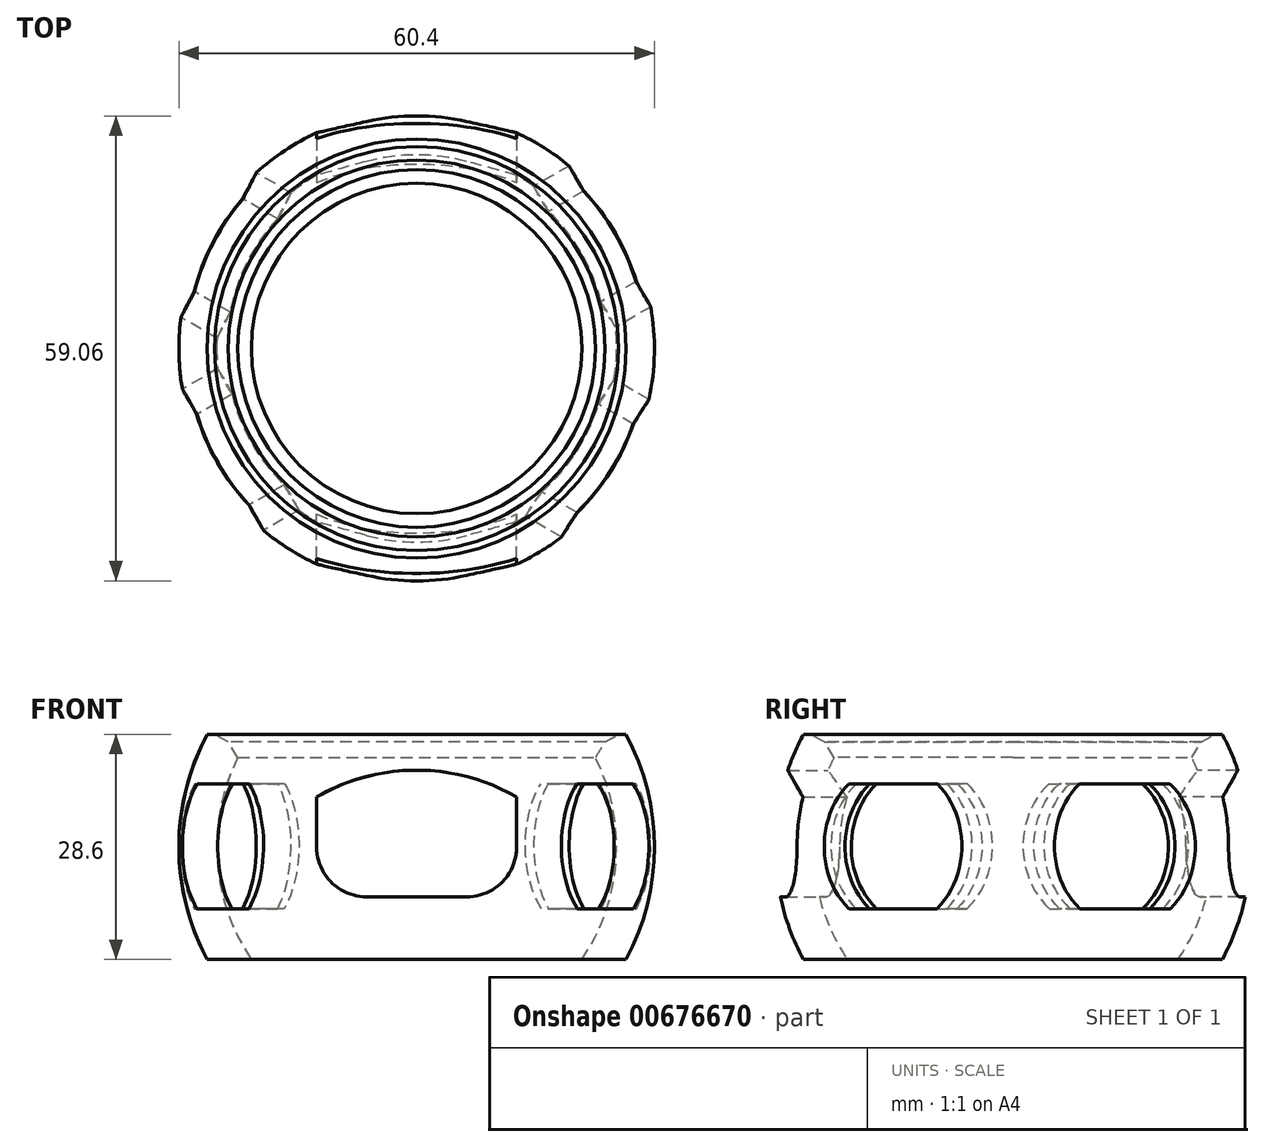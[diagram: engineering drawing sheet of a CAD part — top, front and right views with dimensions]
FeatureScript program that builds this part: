
annotation { "Feature Type Name" : "Feature", "Feature Type Description" : "" }
export const myFeature = defineFeature(function(context is Context, id is Id, definition is map)
    precondition{}
    {
        {
            var Q0;
            Q0=qCreatedBy(makeId("Front.planeOp"),FACE);
            var sketch = newSketch(context, id + "F0", { "sketchPlane" : qUnion([Q0])});
            skArc(sketch, "E0", {"start": v(26.6, -14.3) * mm, "mid": v(30.2, 0) * mm, "end": v(26.6, 14.3) * mm});
            skArc(sketch, "E1", {"start": v(21, -14.3) * mm, "mid": v(25.4, 0) * mm, "end": v(21, 14.3) * mm});
            skLineSegment(sketch, "E2", {"start": v(21, 14.3) * mm, "end": v(26.6, 14.3) * mm});
            skLineSegment(sketch, "E3", {"start": v(21, -14.3) * mm, "end": v(26.6, -14.3) * mm});
            skLineSegment(sketch, "E4", {"start": v(0, 0) * mm, "end": v(0, 43.57) * mm});
            skSolve(sketch);
        }
        {
            var Q0;
            Q0=makeQuery(id+"F0.imprint","IMPRINT",FACE,{"disambiguationData":[TD([[makeQuery(id+"F0.imprint","IMPRINT",EDGE,{"derivedFrom":sQuery(id+"F0.wireOp",EDGE,"E0")}),1.0]])]});
            var Q1;
            Q1=sQuery(id+"F0.wireOp",EDGE,"E4");
            revolve(context, id + "F1", {"entities" : qUnion([Q0]), "axis" : qUnion([Q1]), "revolveType" : RevolveType.FULL});
        }
        {
            var Q0;
            Q0=qCreatedBy(makeId("Top.planeOp"),FACE);
            var sketch = newSketch(context, id + "F2", { "sketchPlane" : qUnion([Q0])});
            skCircle(sketch, "E5", {"center": v(0, 0) * mm, "radius": 23.02 * mm});
            skSolve(sketch);
        }
        {
            var Q0;
            Q0=makeQuery(id+"F1.opRevolve","SWEPT_EDGE",EDGE,{"disambiguationData":[OSD([sQuery(id+"F0.wireOp",EDGE,"E1"),sQuery(id+"F0.wireOp",EDGE,"E2")])]});
            chamfer(context, id + "F3", {"entities" : qUnion([Q0]), "width" : 2.03 * mm, "tangentPropagation" : true});
        }
        {
            var Q0;
            {var subQ0=sQuery(id+"F0.wireOp",EDGE,"E2");Q0=makeQuery(id+"F3.opChamfer","BLEND_EDGE",EDGE,{"blendedFrom":[makeQuery(id+"F1.opRevolve","SWEPT_EDGE",EDGE,{"disambiguationData":[OSD([sQuery(id+"F0.wireOp",EDGE,"E1"),subQ0])]}),makeQuery(id+"F1.opRevolve","SWEPT_FACE",FACE,{"disambiguationData":[OSD([subQ0])]})],"blendedInto":[makeQuery(id+"F1.opRevolve","SWEPT_FACE",FACE,{"disambiguationData":[OSD([subQ0])]})]});}
            chamfer(context, id + "F4", {"entities" : qUnion([Q0]), "width" : 2.03 * mm, "tangentPropagation" : true});
        }
        {
            var Q0;
            Q0=qCreatedBy(makeId("Front.planeOp"),FACE);
            var sketch = newSketch(context, id + "F5", { "sketchPlane" : qUnion([Q0])});
            skLineSegment(sketch, "E6", {"start": v(0, -14.29) * mm, "end": v(0, 0) * mm});
            skLineSegment(sketch, "E7", {"start": v(0, 0) * mm, "end": v(0, -6.35) * mm});
            skLineSegment(sketch, "E8", {"start": v(0, -6.35) * mm, "end": v(6.35, -6.35) * mm});
            skLineSegment(sketch, "E9", {"start": v(0, -6.35) * mm, "end": v(-6.35, -6.35) * mm});
            skLineSegment(sketch, "E10", {"start": v(-12.7, 0) * mm, "end": v(-12.7, 6.35) * mm});
            skLineSegment(sketch, "E11", {"start": v(12.7, 6.35) * mm, "end": v(12.7, 0) * mm});
            skArc(sketch, "E12", {"start": v(12.7, 6.35) * mm, "mid": v(0, 9.75) * mm, "end": v(-12.7, 6.35) * mm});
            skCircle(sketch, "E13", {"center": v(-6.35, 0) * mm, "radius": 6.35 * mm});
            skCircle(sketch, "E14", {"center": v(6.35, 0) * mm, "radius": 6.35 * mm});
            skPoint(sketch, "E15.orphan", {"position": v(-12.7, -6.35) * mm});
            skPoint(sketch, "E16.orphan", {"position": v(12.7, -6.35) * mm});
            skLineSegment(sketch, "E17", {"start": v(0, 0) * mm, "end": v(-1.81, 0) * mm});
            skSolve(sketch);
        }
        {
            var Q0;
            Q0 = qSketchRegion(id + "F5", true);
            extrude(context, id + "F6", {"entities" : qUnion([Q0]), "operationType" : NewBodyOperationType.REMOVE, "oppositeDirection" : true, "depth" : 76.2 * mm, "offsetDistance" : 25.4 * mm});
        }
        {
            var Q0;
            Q0 = qSketchRegion(id + "F5", true);
            extrude(context, id + "F7", {"entities" : qUnion([Q0]), "operationType" : NewBodyOperationType.REMOVE, "depth" : 76.2 * mm, "offsetDistance" : 25.4 * mm});
        }
        {
            var Q0;
            Q0=qCreatedBy(makeId("Top.planeOp"),FACE);
            var sketch = newSketch(context, id + "F8", { "sketchPlane" : qUnion([Q0])});
            skLineSegment(sketch, "E18", {"start": v(41.9, 24.28) * mm, "end": v(-40.53, -23.31) * mm});
            skLineSegment(sketch, "E19", {"start": v(-54.26, 31.56) * mm, "end": v(52.81, -30.26) * mm});
            skLineSegment(sketch, "E20", {"start": v(26.12, 15.16) * mm, "end": v(10, 43.08) * mm});
            skLineSegment(sketch, "E21", {"start": v(26.25, -14.93) * mm, "end": v(7.89, -46.74) * mm});
            skSolve(sketch);
        }
        {
            var Q0;
            Q0=sQuery(id+"F8.wireOp",EDGE,"E20");
            cPlane(context, id + "F9", {"entities" : qUnion([Q0]), "cplaneType" : CPlaneType.LINE_ANGLE, "offset" : 25.4 * mm, "angle" : 90 * degree, "width" : 152.4 * mm, "height" : 152.4 * mm});
        }
        {
            var Q0;
            Q0=qCreatedBy(id+"F9.planeOp",FACE);
            var sketch = newSketch(context, id + "F10", { "sketchPlane" : qUnion([Q0])});
            skArc(sketch, "E22", {"start": v(-6.59, 8.04) * mm, "mid": v(-10.3, 0.1) * mm, "end": v(-6.59, -7.84) * mm});
            skLineSegment(sketch, "E23", {"start": v(0.05, 0.1) * mm, "end": v(0.05, 8.04) * mm});
            skLineSegment(sketch, "E24", {"start": v(0.05, 0.1) * mm, "end": v(0.05, -7.84) * mm});
            skLineSegment(sketch, "E25", {"start": v(0.05, 8.04) * mm, "end": v(-6.59, 8.04) * mm});
            skLineSegment(sketch, "E26", {"start": v(-6.59, 8.04) * mm, "end": v(6.7, 8.04) * mm});
            skLineSegment(sketch, "E27", {"start": v(0.05, -7.84) * mm, "end": v(6.7, -7.84) * mm});
            skLineSegment(sketch, "E28", {"start": v(6.7, -7.84) * mm, "end": v(-6.59, -7.84) * mm});
            skArc(sketch, "E29.trimOffspring", {"start": v(6.7, -7.84) * mm, "mid": v(10.4, 0.1) * mm, "end": v(6.7, 8.04) * mm});
            skSolve(sketch);
        }
        {
            var Q0;
            {var subQ1=sQuery(id+"F10.wireOp",EDGE,"E22");Q0=makeQuery(id+"F10.imprint","IMPRINT",FACE,{"disambiguationData":[TD([[makeQuery(id+"F10.imprint","IMPRINT",EDGE,{"derivedFrom":subQ1}),1.0]])]});}
            var Q1;
            {var subQ4=sQuery(id+"F10.wireOp",EDGE,"E23");Q1=makeQuery(id+"F10.imprint","IMPRINT",FACE,{"disambiguationData":[TD([[makeQuery(id+"F10.imprint","IMPRINT",EDGE,{"derivedFrom":subQ4}),-1.0]])]});}
            var Q2;
            Q2 = qConstructionFilter(qBodyType(qCreatedBy(id + "F10" ,EDGE), BodyType.WIRE), ConstructionObject.NO);
            extrude(context, id + "F11", {"entities" : qUnion([Q0, Q1]), "operationType" : NewBodyOperationType.REMOVE, "surfaceEntities" : qUnion([Q2]), "endBound" : BoundingType.SYMMETRIC, "depth" : 254 * mm, "offsetDistance" : 25.4 * mm});
        }
        {
            var Q0;
            Q0=sQuery(id+"F8.wireOp",EDGE,"E21");
            cPlane(context, id + "F12", {"entities" : qUnion([Q0]), "cplaneType" : CPlaneType.LINE_ANGLE, "offset" : 25.4 * mm, "angle" : 90 * degree, "width" : 152.4 * mm, "height" : 152.4 * mm});
        }
        {
            var Q0;
            Q0=qCreatedBy(id+"F12.planeOp",FACE);
            var sketch = newSketch(context, id + "F13", { "sketchPlane" : qUnion([Q0])});
            skArc(sketch, "E30", {"start": v(-7.85, 8.03) * mm, "mid": v(-11.56, 0.1) * mm, "end": v(-7.85, -7.84) * mm});
            skLineSegment(sketch, "E31", {"start": v(-1.21, 0.1) * mm, "end": v(-1.21, 8.03) * mm});
            skLineSegment(sketch, "E32", {"start": v(-1.21, 0.1) * mm, "end": v(-1.21, -7.84) * mm});
            skLineSegment(sketch, "E33", {"start": v(-1.21, 8.03) * mm, "end": v(-7.85, 8.03) * mm});
            skLineSegment(sketch, "E34", {"start": v(-7.85, 8.03) * mm, "end": v(5.43, 8.03) * mm});
            skLineSegment(sketch, "E35", {"start": v(-1.21, -7.84) * mm, "end": v(5.43, -7.84) * mm});
            skLineSegment(sketch, "E36", {"start": v(5.43, -7.84) * mm, "end": v(-7.85, -7.84) * mm});
            skArc(sketch, "E37.trimOffspring", {"start": v(5.43, -7.84) * mm, "mid": v(9.14, 0.1) * mm, "end": v(5.43, 8.03) * mm});
            skSolve(sketch);
        }
        {
            var Q0;
            {var subQ1=sQuery(id+"F13.wireOp",EDGE,"E30");Q0=makeQuery(id+"F13.imprint","IMPRINT",FACE,{"disambiguationData":[TD([[makeQuery(id+"F13.imprint","IMPRINT",EDGE,{"derivedFrom":subQ1}),1.0]])]});}
            var Q1;
            {var subQ4=sQuery(id+"F13.wireOp",EDGE,"E31");Q1=makeQuery(id+"F13.imprint","IMPRINT",FACE,{"disambiguationData":[TD([[makeQuery(id+"F13.imprint","IMPRINT",EDGE,{"derivedFrom":subQ4}),-1.0]])]});}
            var Q2;
            Q2 = qConstructionFilter(qBodyType(qCreatedBy(id + "F13" ,EDGE), BodyType.WIRE), ConstructionObject.NO);
            extrude(context, id + "F14", {"entities" : qUnion([Q0, Q1]), "operationType" : NewBodyOperationType.REMOVE, "surfaceEntities" : qUnion([Q2]), "endBound" : BoundingType.SYMMETRIC, "depth" : 254 * mm, "offsetDistance" : 25.4 * mm});
        }
    });
